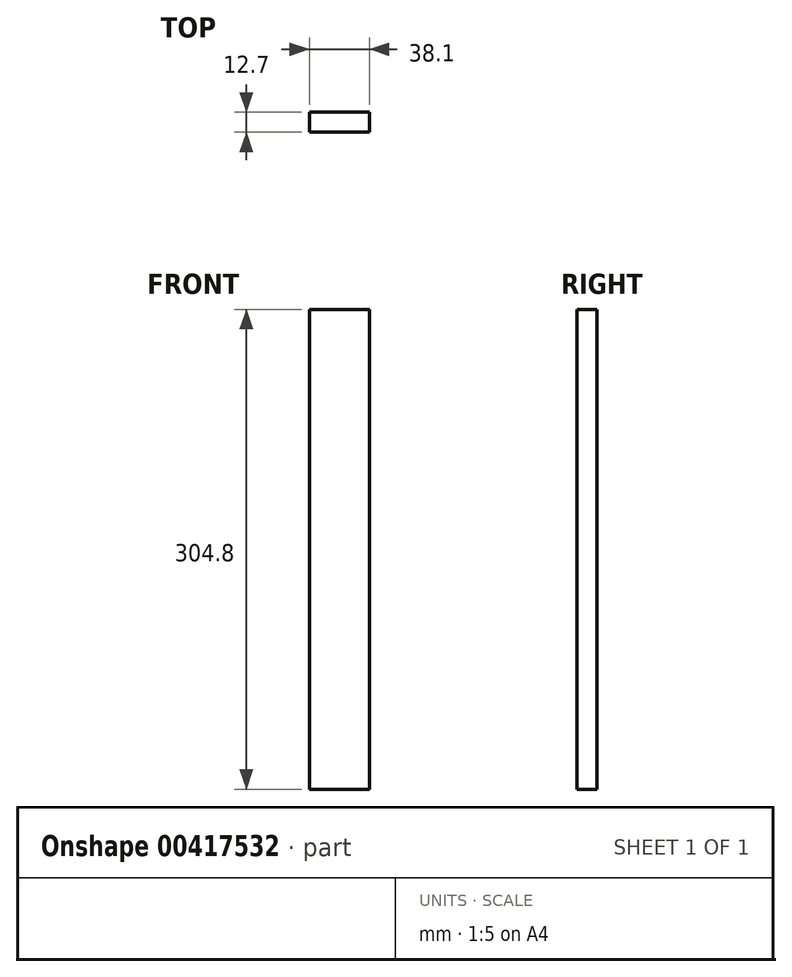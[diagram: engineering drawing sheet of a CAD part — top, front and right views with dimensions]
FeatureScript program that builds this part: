
annotation { "Feature Type Name" : "Feature", "Feature Type Description" : "" }
export const myFeature = defineFeature(function(context is Context, id is Id, definition is map)
    precondition{}
    {
        {
            var Q0;
            Q0=qCreatedBy(makeId("Front.planeOp"),FACE);
            var sketch = newSketch(context, id + "F0", { "sketchPlane" : qUnion([Q0])});
            skLineSegment(sketch, "E0.bottom", {"start": v(-19.05, 152.4) * mm, "end": v(19.05, 152.4) * mm});
            skLineSegment(sketch, "E0.top", {"start": v(-19.05, -152.4) * mm, "end": v(19.05, -152.4) * mm});
            skLineSegment(sketch, "E0.left", {"start": v(-19.05, 152.4) * mm, "end": v(-19.05, -152.4) * mm});
            skLineSegment(sketch, "E0.right", {"start": v(19.05, 152.4) * mm, "end": v(19.05, -152.4) * mm});
            skPoint(sketch, "E0.middle", {"position": v(0, 0) * mm});
            skSolve(sketch);
        }
        {
            var Q0;
            Q0 = qSketchRegion(id + "F0", true);
            extrude(context, id + "F1", {"entities" : qUnion([Q0]), "depth" : 12.7 * mm});
        }
    });
